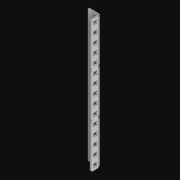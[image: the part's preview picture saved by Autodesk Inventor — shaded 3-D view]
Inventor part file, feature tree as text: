
AUTODESK INVENTOR PART (.ipt)
format: ipt  version: 2021 (Build 250183000, 183)  size: 1,157,632 bytes
history: native  units: in
note: dims shown in document units (in); Inventor stores cm internally (conversion verified against a paired STEP export)
features: extrude x32, other x30, sketch x4, pattern_linear x2, sheet_metal_op x1
ambient origin geometry x8: Origin, YZ Plane, XZ Plane, XY Plane, X Axis, Y Axis, Z Axis, Center Point
bodies: Solid1 (feature_tree)
feature tree (69):
  pattern_linear  "Rectangular Pattern1"  Spacing1=0.5in  [1 undecoded]
  pattern_linear  "Rectangular Pattern3"  Count1=15  [1 undecoded]
  extrude  "Extrusion1"  Depth=0.5in
  extrude  "Extrusion2"  Depth=0.5in
  sketch  "Sketch1"  dims[d0=0.182in]
  other  "Srf1"
  sketch  "Sketch3"  dims[d1=0.063in d2=0.0in]
  other  "Srf3"
  other  "Srf4"
  other  "Srf5"
  other  "Srf6"
  other  "Srf7"
  other  "Srf8"
  other  "Srf9"
  other  "Srf10"
  other  "Srf11"
  other  "Srf12"
  other  "Srf13"
  other  "Srf14"
  other  "Srf15"
  other  "Srf16"
  other  "Srf17"
  other  "Srf142"
  other  "Srf143"
  other  "Srf144"
  other  "Srf145"
  other  "Srf146"
  other  "Srf147"
  other  "Srf148"
  other  "Srf149"
  other  "Srf150"
  other  "Srf151"
  other  "Srf152"
  other  "Srf153"
  other  "Srf154"
  other  "Srf155"
  sketch  "Sketch4"  dims[d6=0.182in]
  sketch  "Sketch5"  dims[d7=0.063in d8=0.0in d11=0.5in d12=0.3937in d14=0.5in d18=5.9055in d20=0.5in d21=10.0in d22=0.0in d23=0.841in d24=0.0in]
  sheet_metal_op  "Fold1"
  extrude  "ExtrusionSrf1"  TaperAngle=0.0deg  [1 undecoded]
  extrude  "ExtrusionSrf3"  Depth=0.5in TaperAngle=0.0deg
  extrude  "ExtrusionSrf4"  [1 undecoded]
  extrude  "ExtrusionSrf5"  [1 undecoded]
  extrude  "ExtrusionSrf6"  [1 undecoded]
  extrude  "ExtrusionSrf7"  [1 undecoded]
  extrude  "ExtrusionSrf8"  [1 undecoded]
  extrude  "ExtrusionSrf9"  [1 undecoded]
  extrude  "ExtrusionSrf10"  [1 undecoded]
  extrude  "ExtrusionSrf11"  [1 undecoded]
  extrude  "ExtrusionSrf12"  [1 undecoded]
  extrude  "ExtrusionSrf13"  [1 undecoded]
  extrude  "ExtrusionSrf14"  [1 undecoded]
  extrude  "ExtrusionSrf15"  [1 undecoded]
  extrude  "ExtrusionSrf16"  [1 undecoded]
  extrude  "ExtrusionSrf17"  [1 undecoded]
  extrude  "ExtrusionSrf142"  [1 undecoded]
  extrude  "ExtrusionSrf143"  [1 undecoded]
  extrude  "ExtrusionSrf144"  [1 undecoded]
  extrude  "ExtrusionSrf145"  [1 undecoded]
  extrude  "ExtrusionSrf146"  [1 undecoded]
  extrude  "ExtrusionSrf147"  [1 undecoded]
  extrude  "ExtrusionSrf148"  [1 undecoded]
  extrude  "ExtrusionSrf149"  [1 undecoded]
  extrude  "ExtrusionSrf150"  [1 undecoded]
  extrude  "ExtrusionSrf151"  [1 undecoded]
  extrude  "ExtrusionSrf152"  [1 undecoded]
  extrude  "ExtrusionSrf153"  [1 undecoded]
  extrude  "ExtrusionSrf154"  [1 undecoded]
  extrude  "ExtrusionSrf155"  [1 undecoded]
note: 31 required parameter values undecoded (feature->parameter linkage not recoverable at this tier; creation-order binding heuristic only, values carry confidence <= 0.55)
